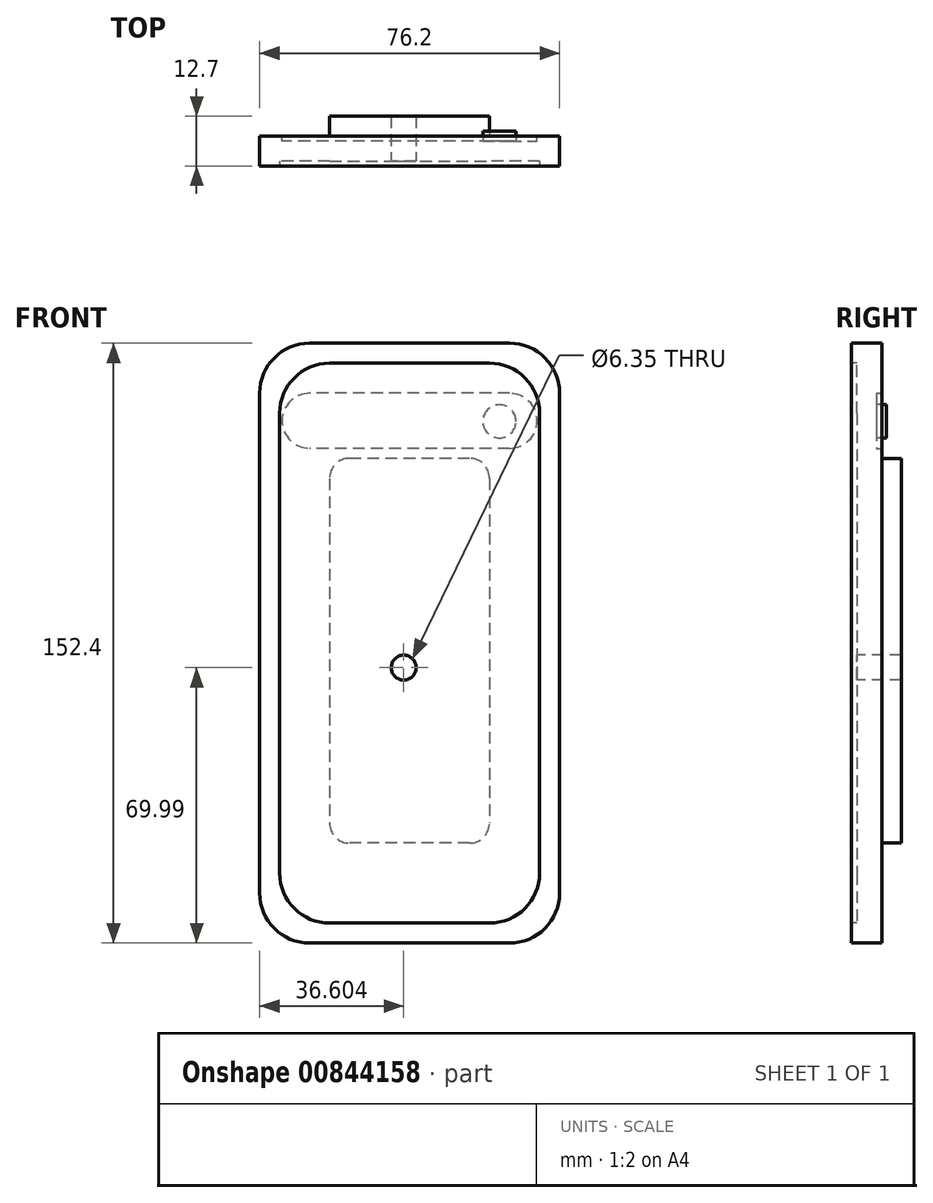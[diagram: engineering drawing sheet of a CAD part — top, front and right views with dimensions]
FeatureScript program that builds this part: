
annotation { "Feature Type Name" : "Feature", "Feature Type Description" : "" }
export const myFeature = defineFeature(function(context is Context, id is Id, definition is map)
    precondition{}
    {
        {
            var Q0;
            Q0=qCreatedBy(makeId("Front.planeOp"),FACE);
            var sketch = newSketch(context, id + "F0", { "sketchPlane" : qUnion([Q0])});
            skLineSegment(sketch, "E0.bottom", {"start": v(-58.06, 95.63) * mm, "end": v(-7.26, 95.63) * mm});
            skLineSegment(sketch, "E0.top", {"start": v(-58.06, -56.77) * mm, "end": v(-7.26, -56.77) * mm});
            skLineSegment(sketch, "E0.left", {"start": v(-70.76, 82.93) * mm, "end": v(-70.76, -44.07) * mm});
            skLineSegment(sketch, "E0.right", {"start": v(5.44, 82.93) * mm, "end": v(5.44, -44.07) * mm});
            skPoint(sketch, "E1.visualSharp", {"position": v(-70.76, 95.63) * mm});
            skArc(sketch, "E1.filletArc", {"start": v(-58.06, 95.63) * mm, "mid": v(-67.04, 91.9) * mm, "end": v(-70.76, 82.93) * mm});
            skPoint(sketch, "E2.visualSharp", {"position": v(5.44, 95.63) * mm});
            skArc(sketch, "E2.filletArc", {"start": v(5.44, 82.93) * mm, "mid": v(1.72, 91.9) * mm, "end": v(-7.26, 95.63) * mm});
            skPoint(sketch, "E3.visualSharp", {"position": v(5.44, -56.77) * mm});
            skArc(sketch, "E3.filletArc", {"start": v(-7.26, -56.77) * mm, "mid": v(1.72, -53.05) * mm, "end": v(5.44, -44.07) * mm});
            skPoint(sketch, "E4.visualSharp", {"position": v(-70.76, -56.77) * mm});
            skArc(sketch, "E4.filletArc", {"start": v(-70.76, -44.07) * mm, "mid": v(-67.04, -53.05) * mm, "end": v(-58.06, -56.77) * mm});
            skSolve(sketch);
        }
        {
            var Q0;
            Q0=makeQuery(id+"F0.imprint","IMPRINT",FACE,{"disambiguationData":[TD([[makeQuery(id+"F0.imprint","IMPRINT",EDGE,{"derivedFrom":sQuery(id+"F0.wireOp",EDGE,"E0.bottom")}),-1.0]])]});
            extrude(context, id + "F1", {"entities" : qUnion([Q0]), "depth" : 7.62 * mm, "offsetDistance" : 25.4 * mm});
        }
        {
            var Q0;
            Q0=makeQuery(id+"F1.opExtrude","CAP_FACE",FACE,{"disambiguationData":[OSD([sQuery(id+"F0.wireOp",EDGE,"E0.bottom"),sQuery(id+"F0.wireOp",EDGE,"E0.top"),sQuery(id+"F0.wireOp",EDGE,"E0.left"),sQuery(id+"F0.wireOp",EDGE,"E0.right"),sQuery(id+"F0.wireOp",EDGE,"E1.filletArc"),sQuery(id+"F0.wireOp",EDGE,"E2.filletArc"),sQuery(id+"F0.wireOp",EDGE,"E3.filletArc"),sQuery(id+"F0.wireOp",EDGE,"E4.filletArc")])],"isStart":true});
            var sketch = newSketch(context, id + "F2", { "sketchPlane" : qUnion([Q0])});
            skLineSegment(sketch, "E5.bottom", {"start": v(7.26, 82.93) * mm, "end": v(58.06, 82.93) * mm});
            skLineSegment(sketch, "E5.top", {"start": v(7.26, 68.93) * mm, "end": v(58.06, 68.93) * mm});
            skLineSegment(sketch, "E5.left", {"start": v(7.26, 82.93) * mm, "end": v(7.26, 68.93) * mm});
            skLineSegment(sketch, "E5.right", {"start": v(58.06, 82.93) * mm, "end": v(58.06, 68.93) * mm});
            skArc(sketch, "E6", {"start": v(7.26, 82.93) * mm, "mid": v(0.26, 75.93) * mm, "end": v(7.26, 68.93) * mm});
            skArc(sketch, "E7", {"start": v(58.06, 68.93) * mm, "mid": v(65.06, 75.93) * mm, "end": v(58.06, 82.93) * mm});
            skSolve(sketch);
        }
        {
            var Q0;
            Q0=makeQuery(id+"F2.imprint","IMPRINT",FACE,{"disambiguationData":[TD([[makeQuery(id+"F2.imprint","IMPRINT",EDGE,{"derivedFrom":sQuery(id+"F2.wireOp",EDGE,"E5.left")}),-1.0]])]});
            var Q1;
            Q1=makeQuery(id+"F2.imprint","IMPRINT",FACE,{"disambiguationData":[TD([[makeQuery(id+"F2.imprint","IMPRINT",EDGE,{"derivedFrom":sQuery(id+"F2.wireOp",EDGE,"E5.bottom")}),-1.0]])]});
            var Q2;
            Q2=makeQuery(id+"F2.imprint","IMPRINT",FACE,{"disambiguationData":[TD([[makeQuery(id+"F2.imprint","IMPRINT",EDGE,{"derivedFrom":sQuery(id+"F2.wireOp",EDGE,"E5.right")}),1.0]])]});
            extrude(context, id + "F3", {"entities" : qUnion([Q0, Q1, Q2]), "operationType" : NewBodyOperationType.REMOVE, "oppositeDirection" : true, "depth" : 1.27 * mm, "offsetDistance" : 25.4 * mm});
        }
        {
            var Q0;
            Q0=makeQuery(id+"F3.boolean.opBoolean","COPY",FACE,{"derivedFrom":makeQuery(id+"F3.opExtrude","CAP_FACE",FACE,{"disambiguationData":[OSD([sQuery(id+"F2.wireOp",EDGE,"E5.bottom"),sQuery(id+"F2.wireOp",EDGE,"E5.top"),sQuery(id+"F2.wireOp",EDGE,"E6"),sQuery(id+"F2.wireOp",EDGE,"E7")])],"isStart":false})});
            var sketch = newSketch(context, id + "F4", { "sketchPlane" : qUnion([Q0])});
            skCircle(sketch, "E8", {"center": v(9.84, 75.79) * mm, "radius": 4.22 * mm});
            skSolve(sketch);
        }
        {
            var Q0;
            Q0=makeQuery(id+"F4.imprint","IMPRINT",FACE,{"disambiguationData":[TD([[makeQuery(id+"F4.imprint","IMPRINT",EDGE,{"derivedFrom":sQuery(id+"F4.wireOp",EDGE,"E8")}),1.0]])]});
            extrude(context, id + "F5", {"entities" : qUnion([Q0]), "operationType" : NewBodyOperationType.ADD, "depth" : 2.54 * mm, "offsetDistance" : 25.4 * mm});
        }
        {
            var Q0;
            Q0=makeQuery(id+"F1.opExtrude","CAP_FACE",FACE,{"disambiguationData":[OSD([sQuery(id+"F0.wireOp",EDGE,"E0.bottom"),sQuery(id+"F0.wireOp",EDGE,"E0.top"),sQuery(id+"F0.wireOp",EDGE,"E0.left"),sQuery(id+"F0.wireOp",EDGE,"E0.right"),sQuery(id+"F0.wireOp",EDGE,"E1.filletArc"),sQuery(id+"F0.wireOp",EDGE,"E2.filletArc"),sQuery(id+"F0.wireOp",EDGE,"E3.filletArc"),sQuery(id+"F0.wireOp",EDGE,"E4.filletArc")])],"isStart":true});
            var sketch = newSketch(context, id + "F6", { "sketchPlane" : qUnion([Q0])});
            skLineSegment(sketch, "E9.bottom", {"start": v(12.34, 66.39) * mm, "end": v(52.98, 66.39) * mm});
            skLineSegment(sketch, "E9.top", {"start": v(12.34, -31.37) * mm, "end": v(52.98, -31.37) * mm});
            skLineSegment(sketch, "E9.left", {"start": v(12.34, 66.39) * mm, "end": v(12.34, -31.37) * mm});
            skLineSegment(sketch, "E9.right", {"start": v(52.98, 66.39) * mm, "end": v(52.98, -31.37) * mm});
            skSolve(sketch);
        }
        {
            var Q0;
            Q0=makeQuery(id+"F6.imprint","IMPRINT",FACE,{"disambiguationData":[TD([[makeQuery(id+"F6.imprint","IMPRINT",EDGE,{"derivedFrom":sQuery(id+"F6.wireOp",EDGE,"E9.bottom")}),-1.0]])]});
            extrude(context, id + "F7", {"entities" : qUnion([Q0]), "operationType" : NewBodyOperationType.ADD, "depth" : 5.08 * mm, "offsetDistance" : 25.4 * mm});
        }
        {
            var Q0;
            Q0=makeQuery(id+"F7.opExtrude","SWEPT_EDGE",EDGE,{"disambiguationData":[OSD([sQuery(id+"F6.wireOp",EDGE,"E9.bottom"),sQuery(id+"F6.wireOp",EDGE,"E9.left")])]});
            var Q1;
            Q1=makeQuery(id+"F7.opExtrude","SWEPT_EDGE",EDGE,{"disambiguationData":[OSD([sQuery(id+"F6.wireOp",EDGE,"E9.bottom"),sQuery(id+"F6.wireOp",EDGE,"E9.right")])]});
            var Q2;
            Q2=makeQuery(id+"F7.opExtrude","SWEPT_EDGE",EDGE,{"disambiguationData":[OSD([sQuery(id+"F6.wireOp",EDGE,"E9.top"),sQuery(id+"F6.wireOp",EDGE,"E9.right")])]});
            var Q3;
            Q3=makeQuery(id+"F7.opExtrude","SWEPT_EDGE",EDGE,{"disambiguationData":[OSD([sQuery(id+"F6.wireOp",EDGE,"E9.top"),sQuery(id+"F6.wireOp",EDGE,"E9.left")])]});
            fillet(context, id + "F8", {"entities" : qUnion([Q0, Q1, Q2, Q3]), "radius" : 5.08 * mm, "tangentPropagation" : true, "allowEdgeOverflow" : false});
        }
        {
            var Q0;
            Q0=makeQuery(id+"F1.opExtrude","CAP_FACE",FACE,{"disambiguationData":[OSD([sQuery(id+"F0.wireOp",EDGE,"E0.bottom"),sQuery(id+"F0.wireOp",EDGE,"E0.top"),sQuery(id+"F0.wireOp",EDGE,"E0.left"),sQuery(id+"F0.wireOp",EDGE,"E0.right"),sQuery(id+"F0.wireOp",EDGE,"E1.filletArc"),sQuery(id+"F0.wireOp",EDGE,"E2.filletArc"),sQuery(id+"F0.wireOp",EDGE,"E3.filletArc"),sQuery(id+"F0.wireOp",EDGE,"E4.filletArc")])],"isStart":false});
            var sketch = newSketch(context, id + "F9", { "sketchPlane" : qUnion([Q0])});
            skLineSegment(sketch, "E10.bottom", {"start": v(-52.98, 90.55) * mm, "end": v(-12.34, 90.55) * mm});
            skLineSegment(sketch, "E10.top", {"start": v(-52.98, -51.7) * mm, "end": v(-12.34, -51.7) * mm});
            skLineSegment(sketch, "E10.left", {"start": v(-65.68, 77.85) * mm, "end": v(-65.68, -39) * mm});
            skLineSegment(sketch, "E10.right", {"start": v(0.36, 77.85) * mm, "end": v(0.36, -39) * mm});
            skPoint(sketch, "E11.visualSharp", {"position": v(-65.68, 90.55) * mm});
            skArc(sketch, "E11.filletArc", {"start": v(-52.98, 90.55) * mm, "mid": v(-61.96, 86.83) * mm, "end": v(-65.68, 77.85) * mm});
            skPoint(sketch, "E12.visualSharp", {"position": v(0.36, 90.55) * mm});
            skArc(sketch, "E12.filletArc", {"start": v(0.36, 77.85) * mm, "mid": v(-3.36, 86.83) * mm, "end": v(-12.34, 90.55) * mm});
            skPoint(sketch, "E13.visualSharp", {"position": v(0.36, -51.7) * mm});
            skArc(sketch, "E13.filletArc", {"start": v(-12.34, -51.7) * mm, "mid": v(-3.36, -47.97) * mm, "end": v(0.36, -39) * mm});
            skPoint(sketch, "E14.visualSharp", {"position": v(-65.68, -51.7) * mm});
            skArc(sketch, "E14.filletArc", {"start": v(-65.68, -39) * mm, "mid": v(-61.96, -47.97) * mm, "end": v(-52.98, -51.7) * mm});
            skSolve(sketch);
        }
        {
            var Q0;
            Q0=makeQuery(id+"F9.imprint","IMPRINT",FACE,{"disambiguationData":[TD([[makeQuery(id+"F9.imprint","IMPRINT",EDGE,{"derivedFrom":sQuery(id+"F9.wireOp",EDGE,"E10.bottom")}),-1.0]])]});
            extrude(context, id + "F10", {"entities" : qUnion([Q0]), "operationType" : NewBodyOperationType.REMOVE, "oppositeDirection" : true, "depth" : 1.27 * mm, "offsetDistance" : 25.4 * mm});
        }
        {
            var Q0;
            Q0=makeQuery(id+"F10.boolean.opBoolean","COPY",FACE,{"derivedFrom":makeQuery(id+"F10.opExtrude","CAP_FACE",FACE,{"disambiguationData":[OSD([sQuery(id+"F9.wireOp",EDGE,"E10.bottom"),sQuery(id+"F9.wireOp",EDGE,"E10.top"),sQuery(id+"F9.wireOp",EDGE,"E10.left"),sQuery(id+"F9.wireOp",EDGE,"E10.right"),sQuery(id+"F9.wireOp",EDGE,"E11.filletArc"),sQuery(id+"F9.wireOp",EDGE,"E12.filletArc"),sQuery(id+"F9.wireOp",EDGE,"E13.filletArc"),sQuery(id+"F9.wireOp",EDGE,"E14.filletArc")])],"isStart":false})});
            var sketch = newSketch(context, id + "F11", { "sketchPlane" : qUnion([Q0])});
            skPoint(sketch, "E15", {"position": v(-34.16, 13.22) * mm});
            skSolve(sketch);
        }
        {
            var Q0;
            Q0=sQuery(id+"F11.wireOp",VERTEX,"E15");
            var Q1;
            Q1=makeQuery(id+"F1.opExtrude","SWEPT_BODY",BODY,{"disambiguationData":[OSD([sQuery(id+"F0.wireOp",EDGE,"E0.bottom"),sQuery(id+"F0.wireOp",EDGE,"E0.top"),sQuery(id+"F0.wireOp",EDGE,"E0.left"),sQuery(id+"F0.wireOp",EDGE,"E0.right"),sQuery(id+"F0.wireOp",EDGE,"E1.filletArc"),sQuery(id+"F0.wireOp",EDGE,"E2.filletArc"),sQuery(id+"F0.wireOp",EDGE,"E3.filletArc"),sQuery(id+"F0.wireOp",EDGE,"E4.filletArc")])]});
            hole(context, id + "F12", {"style" : HoleStyle.SIMPLE, "endStyle" : HoleEndStyle.THROUGH, "holeDiameter" : 6.35 * mm, "majorDiameter" : 6.35 * mm, "isTappedThrough" : true, "tappedDepth" : 12.7 * mm, "tapClearance" : 3, "locations" : qUnion([Q0]), "scope" : qUnion([Q1])});
        }
    });
